# Revit family: NAU_NaughtOne_Stng_Percy
name_source: partatom
category: Furniture
units: mm (PartAtom-declared; Revit-internal decimal feet)

## family parameters
Always vertical = Yes
Cut with Voids When Loaded = No
OmniClass Number = 23.40.20.00
OmniClass Title = General Furniture and Specialties
Room Calculation Point = No
Shared = Yes
Work Plane-Based = No

## types (1)
- NOPRC10 - Percy Lounge Chair
    Assembly Code = E2020200
    AssetType = Movable
    BIMObjectName = NAU_NaughtOne_Seating_Percy
    Category = Pr_40_50_12 : Chairs, seats and benches
    Color = Various
    Default Elevation = 0 mm  [stored 0 ft]
    Description = Percy Lounge Chair
    DurationUnit = year
    Features = Textile available in any of NaughtOne standard offering or COM. 16 standard RALs available for steel frame
    Finish = Textile and Steel in RAL.
    FootMaterial = NAU_Generic_Plastic_Black
    HighestSeatingHeight = 460 mm  [stored 1.50919 ft]
    IfcExportAs = IfcFurnishingElementType
    IfcExportType = CHAIR
    Keynote = Pr_40_50_12
    LowestSeatingHeight = 460 mm  [stored 1.50919 ft]
    MainColor = Various
    ManufacturerAddress = Unit D, Knaresborough Technology Park, Manse Lane, Knaresborough, HG5 8LF
    ManufacturerName = NaughtOne
    ManufacturerURL = www.naughtone.com/
    Material = Textile. Steel in powdercoat
    Model = NOPRC10
    ModelNumber = NOPRC10
    ModelReference = Percy Lounge Chair
    NBSDescription = Seating
    NBSReference = 45-35-72/352
    Name = Seating_Percy_NaughtOne
    NominalHeight = 760 mm  [stored 2.49344 ft]
    NominalLength = 760 mm  [stored 2.49344 ft]
    NominalWidth = 700 mm  [stored 2.29659 ft]
    ProductInformation = www.naughtone.com/products/
    SeatingHeight = 460 mm  [stored 1.50919 ft]
    Shape = Rectangular
    Size = 760 x 700 x 760mm
    SustainabilityPerformance = FSC certifeied, SCS indoor advantage gold
    URL = www.naughtone.com
    Uniclass2015Code = Pr_40_50_12
    Uniclass2015Title = Chairs, seats and benches
    Version = 1
    WarrantyDescription = Request warranty information from NaughtOne
    WarrantyDurationLabor = 10
    WarrantyDurationParts = 10
    WarrantyDurationUnit = year

note: [stored X ft] marks values corroborated as IEEE doubles in the binary element streams (Revit-internal decimal feet)

## geometry (parser evidence)
native form markers: Sweep x2
no freeform markers — native parametric forms only
